# Revit family: Gira_291103
name_source: partatom
category: Electrical Fixtures
revit_build: Autodesk Revit 2017 (Build: 20160225_1515(x64)
units: mm (PartAtom-declared; Revit-internal decimal feet)

## family parameters
Cut with Voids When Loaded = No
Host = Face
Maintain Annotation Orientation = Yes
Part Type = Normal
Room Calculation Point = No
Round Connector Dimension = Use Diameter
Shared = No

## types (1)
- Sw-off btn System 55 p.white
    Available = No
    BIM (1) = https://media.stage.bim.site und Tasten.rfa?public/gira/36a6b08/Sys55_Komplettgerät_Schalten und Tasten.rfa
    Button function = Quit call
    Category = Call-/control unit clinic-installation
    Colour push button = Green
    Construction = Wall model
    Data sheet (1) = https://katalog.gira.de
    Default Elevation = 1219 mm
    Description = Sw-off btn Sys55 PW,Switch-off button,System 55,pure white glossy,Features:,- Calls are switched off using the green switch-off button.
    GTIN = 4010337062349
    HAN = 291103
    HeinzeBIM = https://bimportal.heinze.de
    Manufacturer = Gira
    Manufacturer URL = https://www.gira.de
    Model = Sys55_Komplettgerät_Schalten und Tasten
    Name = Sw-off btn System 55 p.white
    Suitable for = Call
    Suitable for bus connection = 2-wire
    URL = http://katalog.gira.de

## geometry (parser evidence)
native form markers: Blend x2, Sweep x10
no freeform markers — native parametric forms only
